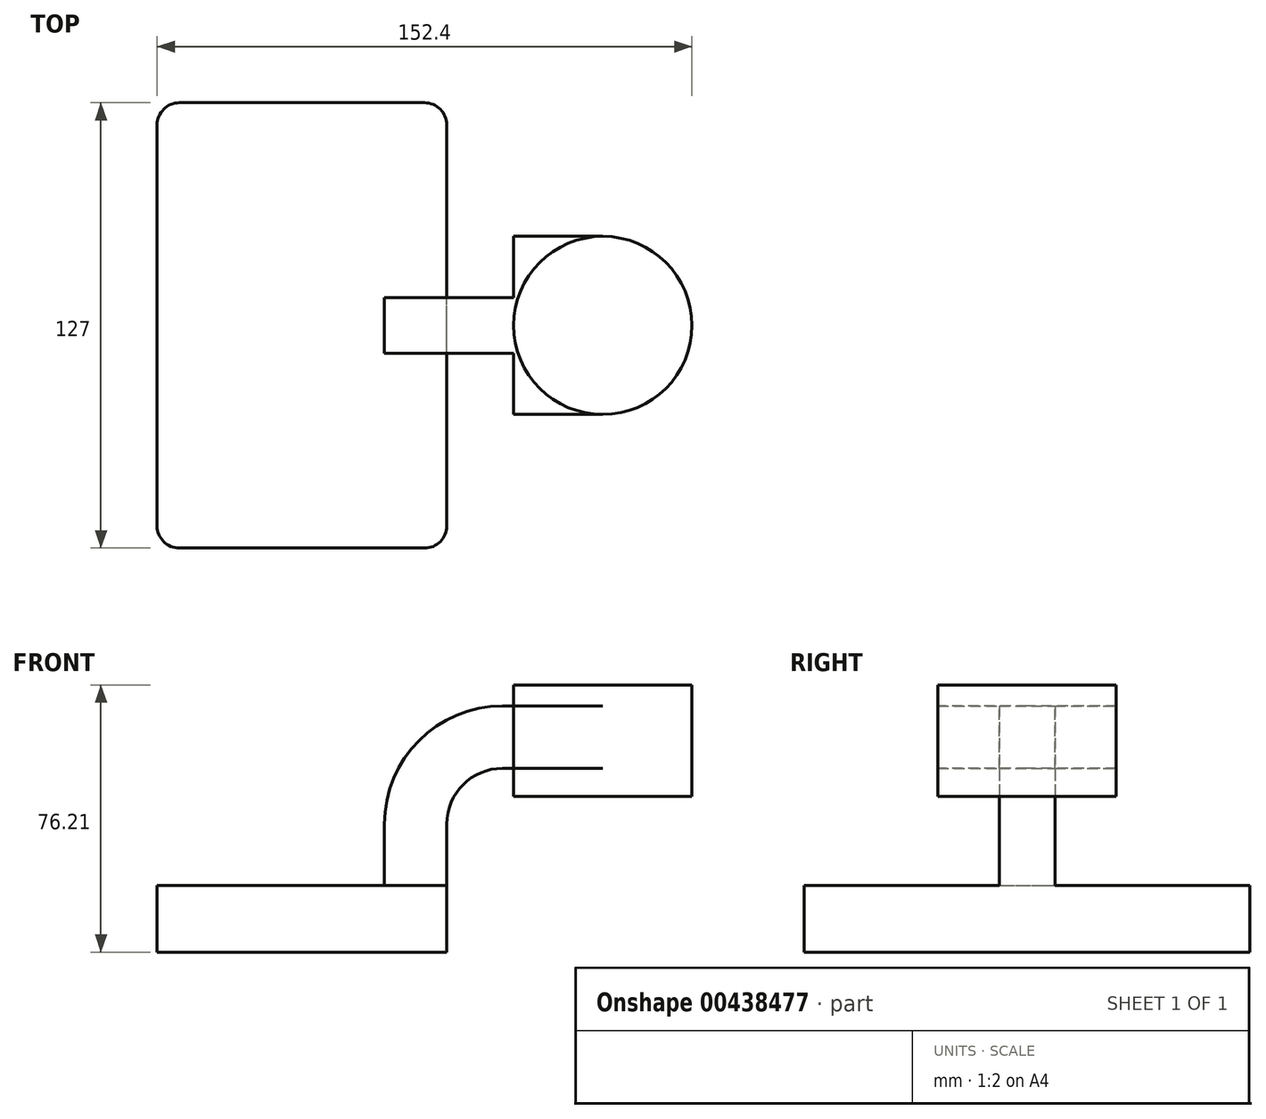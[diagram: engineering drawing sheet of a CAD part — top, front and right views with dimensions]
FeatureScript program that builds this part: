
annotation { "Feature Type Name" : "Feature", "Feature Type Description" : "" }
export const myFeature = defineFeature(function(context is Context, id is Id, definition is map)
    precondition{}
    {
        {
            var Q0;
            Q0=qCreatedBy(makeId("Front.planeOp"),FACE);
            var sketch = newSketch(context, id + "F0", { "sketchPlane" : qUnion([Q0])});
            skLineSegment(sketch, "E0.bottom", {"start": v(-41.27, -9.53) * mm, "end": v(41.28, -9.53) * mm});
            skLineSegment(sketch, "E0.top", {"start": v(-41.28, 9.53) * mm, "end": v(41.28, 9.53) * mm});
            skLineSegment(sketch, "E0.left", {"start": v(-41.28, -9.53) * mm, "end": v(-41.28, 9.53) * mm});
            skLineSegment(sketch, "E0.right", {"start": v(41.28, -9.53) * mm, "end": v(41.28, 9.52) * mm});
            skPoint(sketch, "E0.middle", {"position": v(0, 0) * mm});
            skLineSegment(sketch, "E1.bottom", {"start": v(60.33, 34.93) * mm, "end": v(111.13, 34.93) * mm});
            skLineSegment(sketch, "E1.top", {"start": v(60.33, 66.67) * mm, "end": v(111.13, 66.67) * mm});
            skLineSegment(sketch, "E1.left", {"start": v(60.33, 34.93) * mm, "end": v(60.33, 66.67) * mm});
            skLineSegment(sketch, "E1.right", {"start": v(111.13, 34.93) * mm, "end": v(111.13, 66.67) * mm});
            skPoint(sketch, "E1.middle", {"position": v(85.73, 50.8) * mm});
            skLineSegment(sketch, "E2.bottom", {"start": v(41.27, 27) * mm, "end": v(41.27, 27) * mm});
            skLineSegment(sketch, "E2.top", {"start": v(41.28, -7.95) * mm, "end": v(41.28, -7.95) * mm});
            skLineSegment(sketch, "E2.left", {"start": v(41.27, 27) * mm, "end": v(41.27, -7.95) * mm});
            skLineSegment(sketch, "E2.right", {"start": v(41.28, 27) * mm, "end": v(41.28, -7.95) * mm});
            skPoint(sketch, "E2.middle", {"position": v(41.28, 9.52) * mm});
            skArc(sketch, "E3", {"start": v(41.27, 27) * mm, "mid": v(45.92, 38.23) * mm, "end": v(57.15, 42.88) * mm});
            skPoint(sketch, "E4.endSnap0", {"position": v(85.73, 34.93) * mm});
            skPoint(sketch, "E5.endSnap0", {"position": v(60.33, 50.8) * mm});
            skLineSegment(sketch, "E6", {"start": v(57.15, 42.88) * mm, "end": v(85.73, 42.88) * mm});
            skLineSegment(sketch, "E7", {"start": v(41.28, 9.53) * mm, "end": v(41.28, 27) * mm});
            skArc(sketch, "E8.0", {"start": v(23.5, 27) * mm, "mid": v(33.35, 50.8) * mm, "end": v(57.15, 60.66) * mm});
            skLineSegment(sketch, "E9", {"start": v(23.5, 27) * mm, "end": v(23.5, 9.52) * mm});
            skLineSegment(sketch, "E10", {"start": v(57.15, 60.66) * mm, "end": v(60.33, 60.66) * mm});
            skFitSpline(sketch, "E11", {"points": [v(-41.27, 9.53) * mm, v(57.15, 60.66) * mm], "startDerivative": vector(0.4, 70.67) * mm, "endDerivative": vector(135.7, -1.23) * mm});
            skLineSegment(sketch, "E12", {"start": v(85.73, 34.93) * mm, "end": v(85.73, 66.67) * mm});
            skLineSegment(sketch, "E13", {"start": v(60.33, 60.66) * mm, "end": v(85.73, 60.66) * mm});
            skSolve(sketch);
        }
        {
            var Q0;
            Q0=makeQuery(id+"F0.imprint","IMPRINT",FACE,{"disambiguationData":[TD([[makeQuery(id+"F0.imprint","IMPRINT",EDGE,{"derivedFrom":sQuery(id+"F0.wireOp",EDGE,"E0.bottom")}),1.0]])]});
            extrude(context, id + "F1", {"entities" : qUnion([Q0]), "depth" : 127 * mm, "symmetric" : true});
        }
        {
            var Q0;
            {var subQ0=sQuery(id+"F0.wireOp",EDGE,"E3");Q0=makeQuery(id+"F0.imprint","IMPRINT",FACE,{"disambiguationData":[TD([[makeQuery(id+"F0.imprint","IMPRINT",EDGE,{"derivedFrom":subQ0}),1.0]])]});}
            var Q1;
            {var subQ0=sQuery(id+"F0.wireOp",EDGE,"E13");Q1=makeQuery(id+"F0.imprint","IMPRINT",FACE,{"disambiguationData":[TD([[makeQuery(id+"F0.imprint","IMPRINT",EDGE,{"derivedFrom":subQ0}),-1.0]])]});}
            extrude(context, id + "F2", {"entities" : qUnion([Q0, Q1]), "operationType" : NewBodyOperationType.ADD, "depth" : 50.8 * mm, "symmetric" : true});
        }
        {
            var Q0;
            Q0=makeQuery(id+"F0.imprint","IMPRINT",FACE,{"disambiguationData":[TD([[makeQuery(id+"F0.imprint","IMPRINT",EDGE,{"derivedFrom":sQuery(id+"F0.wireOp",EDGE,"E8.0")}),1.0]])]});
            extrude(context, id + "F3", {"entities" : qUnion([Q0]), "operationType" : NewBodyOperationType.ADD, "depth" : 15.88 * mm, "symmetric" : true});
        }
        {
            var Q0;
            {var subQ4=sQuery(id+"F0.wireOp",EDGE,"E1.right");Q0=makeQuery(id+"F0.imprint","IMPRINT",FACE,{"disambiguationData":[TD([[makeQuery(id+"F0.imprint","IMPRINT",EDGE,{"derivedFrom":subQ4}),1.0]])]});}
            var Q1;
            Q1=sQuery(id+"F0.wireOp",EDGE,"E12");
            revolve(context, id + "F4", {"operationType" : NewBodyOperationType.ADD, "entities" : qUnion([Q0]), "axis" : qUnion([Q1]), "revolveType" : RevolveType.FULL});
        }
        {
            var Q0;
            Q0=makeQuery(id+"F1.opExtrude","CAP_EDGE",EDGE,{"disambiguationData":[OSD([sQuery(id+"F0.wireOp",EDGE,"E0.right"),sQuery(id+"F0.wireOp",EDGE,"E2.right")])],"isStart":false});
            var Q1;
            Q1=makeQuery(id+"F1.opExtrude","CAP_EDGE",EDGE,{"disambiguationData":[OSD([sQuery(id+"F0.wireOp",EDGE,"E0.left")])],"isStart":false});
            var Q2;
            Q2=makeQuery(id+"F1.opExtrude","CAP_EDGE",EDGE,{"disambiguationData":[OSD([sQuery(id+"F0.wireOp",EDGE,"E0.right"),sQuery(id+"F0.wireOp",EDGE,"E2.right")])],"isStart":true});
            var Q3;
            Q3=makeQuery(id+"F1.opExtrude","CAP_EDGE",EDGE,{"disambiguationData":[OSD([sQuery(id+"F0.wireOp",EDGE,"E0.left")])],"isStart":true});
            fillet(context, id + "F5", {"entities" : qUnion([Q0, Q1, Q2, Q3]), "radius" : 6.35 * mm, "tangentPropagation" : true, "allowEdgeOverflow" : false});
        }
    });
